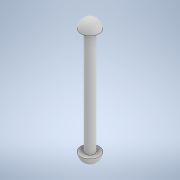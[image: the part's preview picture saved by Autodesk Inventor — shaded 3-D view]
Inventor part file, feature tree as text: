
AUTODESK INVENTOR PART (.ipt)
format: ipt  version: 2021 (Build 250183000, 183)  size: 136,704 bytes
history: native  units: mm
features: sketch x5, extrude x2, revolve x2
ambient origin geometry x8: Origin, YZ Plane, XZ Plane, XY Plane, X Axis, Y Axis, Z Axis, Center Point
bodies: Solid1 (feature_tree)
feature tree (9):
  extrude  "Extrusion1"  Depth=70.0mm TaperAngle=0.0deg
  sketch  "Sketch2"  dims[d3=9.0mm d4=9.0mm]
  revolve  "Revolution1"  [1 undecoded]
  extrude  "Extrusion2"  TaperAngle=90.0deg  [1 undecoded]
  revolve  "Revolution2"  [1 undecoded]
  sketch  "Sketch1"  dims[d0=6.0mm d1=70.0mm d2=0.0mm]
  sketch  "Sketch3"  dims[d5=9.0mm d6=90.0deg]
  sketch  "Sketch4"  dims[d7=20.0mm d8=0.0mm d9=6.0mm]
  sketch  "Sketch5"  dims[d10=6.0mm d11=6.0mm d12=6.0mm d13=90.0deg]
note: 3 required parameter values undecoded (feature->parameter linkage not recoverable at this tier; creation-order binding heuristic only, values carry confidence <= 0.55)